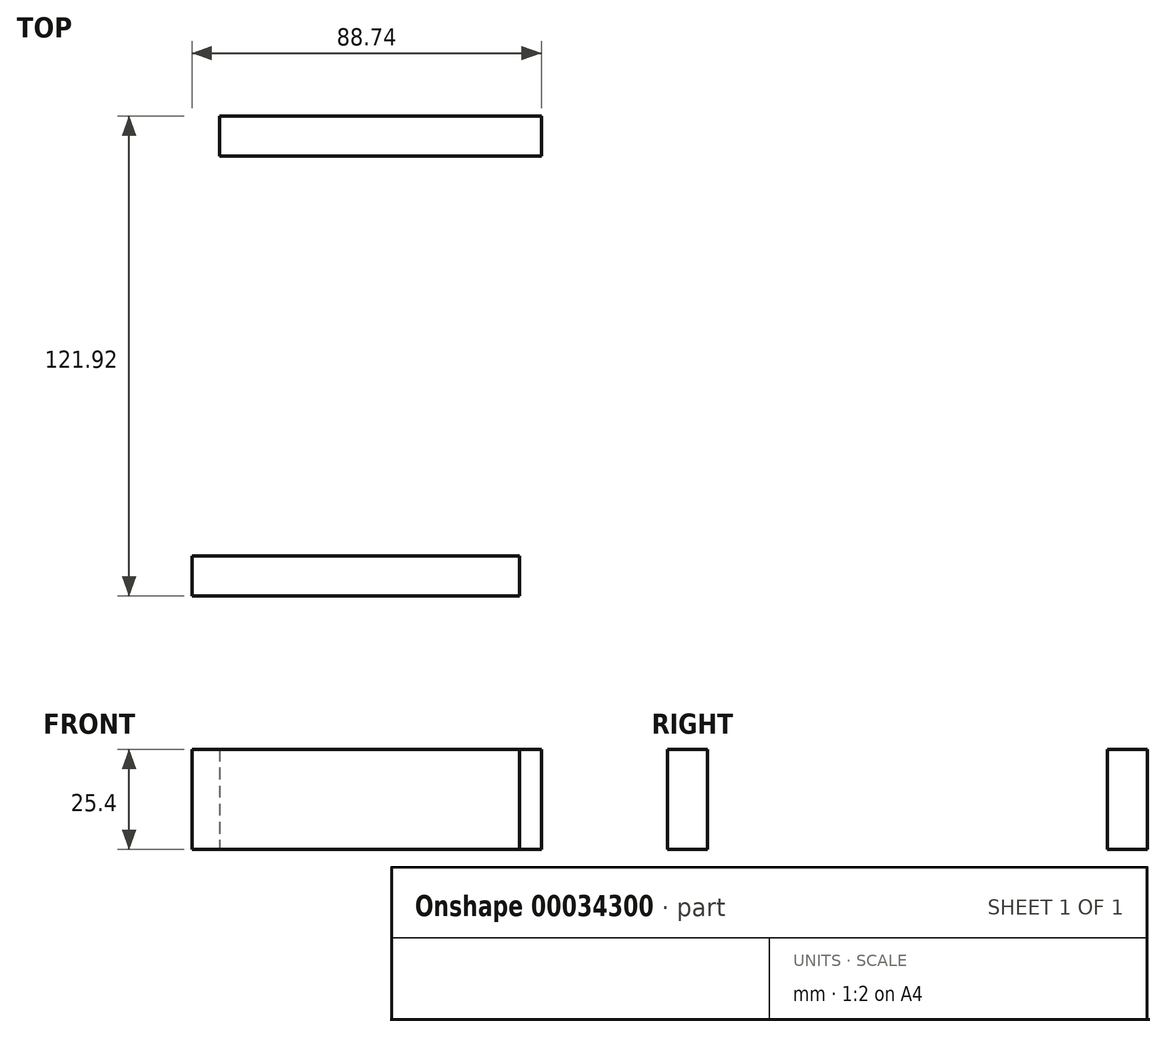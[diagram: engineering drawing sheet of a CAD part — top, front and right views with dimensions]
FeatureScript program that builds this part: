
annotation { "Feature Type Name" : "Feature", "Feature Type Description" : "" }
export const myFeature = defineFeature(function(context is Context, id is Id, definition is map)
    precondition{}
    {
        {
            var Q0;
            Q0=qCreatedBy(makeId("Top.planeOp"),FACE);
            var sketch = newSketch(context, id + "F0", { "sketchPlane" : qUnion([Q0])});
            skLineSegment(sketch, "E0.bottom", {"start": v(43.9, 31.53) * mm, "end": v(-32.3, 31.53) * mm});
            skLineSegment(sketch, "E0.top", {"start": v(43.9, -70.07) * mm, "end": v(-32.3, -70.07) * mm});
            skLineSegment(sketch, "E0.left", {"start": v(43.9, 31.53) * mm, "end": v(43.9, -70.07) * mm});
            skLineSegment(sketch, "E0.right", {"start": v(-32.3, 31.53) * mm, "end": v(-32.3, -70.07) * mm});
            skLineSegment(sketch, "E1.bottom", {"start": v(43.9, 31.53) * mm, "end": v(49.48, 31.53) * mm});
            skLineSegment(sketch, "E1.top", {"start": v(43.9, 41.69) * mm, "end": v(49.48, 41.69) * mm});
            skLineSegment(sketch, "E1.left", {"start": v(43.9, 31.53) * mm, "end": v(43.9, 41.69) * mm});
            skLineSegment(sketch, "E1.right", {"start": v(49.48, 31.53) * mm, "end": v(49.48, 41.69) * mm});
            skLineSegment(sketch, "E2.bottom", {"start": v(49.48, 31.53) * mm, "end": v(43.9, 31.53) * mm});
            skLineSegment(sketch, "E2.top", {"start": v(49.48, -80.23) * mm, "end": v(43.9, -80.23) * mm});
            skLineSegment(sketch, "E2.left", {"start": v(49.48, 31.53) * mm, "end": v(49.48, -80.23) * mm});
            skLineSegment(sketch, "E2.right", {"start": v(43.9, 31.53) * mm, "end": v(43.9, -80.23) * mm});
            skLineSegment(sketch, "E3.bottom", {"start": v(49.48, -80.23) * mm, "end": v(-39.26, -80.23) * mm});
            skLineSegment(sketch, "E3.top", {"start": v(49.48, -70.07) * mm, "end": v(-39.26, -70.07) * mm});
            skLineSegment(sketch, "E3.left", {"start": v(49.48, -80.23) * mm, "end": v(49.48, -70.07) * mm});
            skLineSegment(sketch, "E3.right", {"start": v(-39.26, -80.23) * mm, "end": v(-39.26, -70.07) * mm});
            skPoint(sketch, "E4.oppositeSnap0", {"position": v(-39.26, -75.15) * mm});
            skLineSegment(sketch, "E4.bottom", {"start": v(-32.3, -70.07) * mm, "end": v(-39.26, -70.07) * mm});
            skLineSegment(sketch, "E4.left", {"start": v(-32.3, -70.07) * mm, "end": v(-32.3, 41.69) * mm});
            skLineSegment(sketch, "E4.right", {"start": v(-39.26, -70.07) * mm, "end": v(-39.26, 41.69) * mm});
            skLineSegment(sketch, "E5.bottom", {"start": v(43.9, 41.69) * mm, "end": v(-32.3, 41.69) * mm});
            skLineSegment(sketch, "E5.left", {"start": v(43.9, 41.69) * mm, "end": v(43.9, 31.53) * mm});
            skLineSegment(sketch, "E5.right", {"start": v(-32.3, 41.69) * mm, "end": v(-32.3, 31.53) * mm});
            skLineSegment(sketch, "E6", {"start": v(-32.3, 41.69) * mm, "end": v(-39.26, 41.69) * mm});
            skPoint(sketch, "E7.orphan", {"position": v(-39.26, 39.48) * mm});
            skSolve(sketch);
        }
        {
            var Q0;
            Q0=makeQuery(id+"F0.imprint","IMPRINT",FACE,{"disambiguationData":[TD([[makeQuery(id+"F0.imprint","IMPRINT",EDGE,{"derivedFrom":sQuery(id+"F0.wireOp",EDGE,"E5.bottom")}),1.0]])]});
            extrude(context, id + "F1", {"entities" : qUnion([Q0]), "depth" : 25.4 * mm});
        }
        {
            var Q0;
            Q0=makeQuery(id+"F0.imprint","IMPRINT",FACE,{"disambiguationData":[TD([[makeQuery(id+"F0.imprint","IMPRINT",EDGE,{"derivedFrom":sQuery(id+"F0.wireOp",EDGE,"E4.bottom")}),-1.0]])]});
            var Q1;
            {var subQ0=sQuery(id+"F0.wireOp",EDGE,"E2.bottom");Q1=makeQuery(id+"F0.imprint","IMPRINT",FACE,{"disambiguationData":[TD([[makeQuery(id+"F0.imprint","IMPRINT",EDGE,{"derivedFrom":subQ0}),1.0]])]});}
            var Q2;
            Q2=makeQuery(id+"F0.imprint","IMPRINT",FACE,{"disambiguationData":[TD([[makeQuery(id+"F0.imprint","IMPRINT",EDGE,{"derivedFrom":sQuery(id+"F0.wireOp",EDGE,"E1.top")}),-1.0]])]});
            var Q3;
            {var subQ5=sQuery(id+"F0.wireOp",EDGE,"E3.left");Q3=makeQuery(id+"F0.imprint","IMPRINT",FACE,{"disambiguationData":[TD([[makeQuery(id+"F0.imprint","IMPRINT",EDGE,{"derivedFrom":subQ5}),1.0]])]});}
            var Q4;
            {var subQ0=sQuery(id+"F0.wireOp",EDGE,"E3.right");Q4=makeQuery(id+"F0.imprint","IMPRINT",FACE,{"disambiguationData":[TD([[makeQuery(id+"F0.imprint","IMPRINT",EDGE,{"derivedFrom":subQ0}),-1.0]])]});}
            extrude(context, id + "F2", {"entities" : qUnion([Q0, Q1, Q2, Q3, Q4]), "operationType" : NewBodyOperationType.ADD, "depth" : 25.4 * mm});
        }
    });
